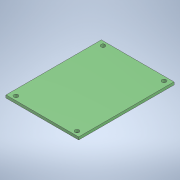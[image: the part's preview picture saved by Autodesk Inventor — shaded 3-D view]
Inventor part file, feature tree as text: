
AUTODESK INVENTOR PART (.ipt)
format: ipt  version: 2022 (Build 260153000, 153)  size: 371,200 bytes
history: native  units: in
note: dims shown in document units (in); Inventor stores cm internally (conversion verified against a paired STEP export)
features: sketch x3, extrude x1, hole x1, emboss x1
ambient origin geometry x8: Origin, YZ Plane, XZ Plane, XY Plane, X Axis, Y Axis, Z Axis, Center Point
bodies: Solid1 (feature_tree)
feature tree (6):
  extrude  "Extrusion1"  Depth=2.2205in
  hole  "Hole1"  [1 undecoded]
  emboss  "Emboss2"
  sketch  "Sketch1"  dims[d0=1.6929in d1=2.2205in]
  sketch  "Sketch2"  dims[d2=0.063in d3=0.0in]
  sketch  "Sketch4"  dims[d8=0.0984in d9=0.75in d10=0.119in d11=0.25in d12=0.5635in d13=1.0in d14=0.8108in d17=0.002in d18=0.0in d19=1.4213in d20=2.0276in d21=1.0138in d22=0.7106in]
note: 1 required parameter value undecoded (feature->parameter linkage not recoverable at this tier; creation-order binding heuristic only, values carry confidence <= 0.55)
